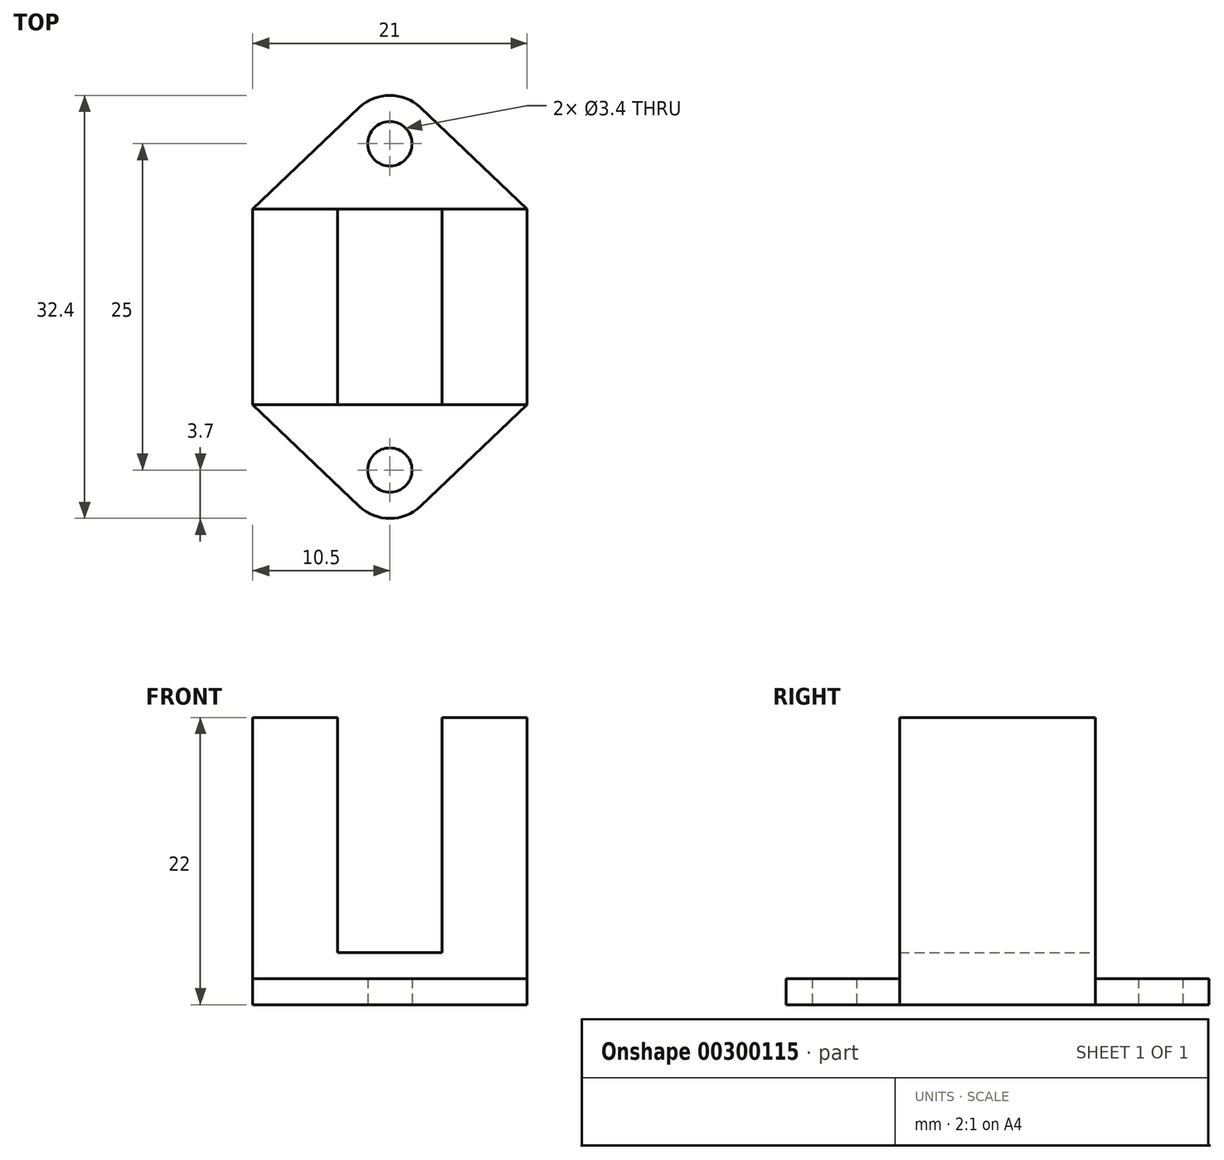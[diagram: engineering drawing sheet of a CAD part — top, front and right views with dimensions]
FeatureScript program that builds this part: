
annotation { "Feature Type Name" : "Feature", "Feature Type Description" : "" }
export const myFeature = defineFeature(function(context is Context, id is Id, definition is map)
    precondition{}
    {
        {
            var Q0;
            Q0=qCreatedBy(makeId("Top.planeOp"),FACE);
            var sketch = newSketch(context, id + "F0", { "sketchPlane" : qUnion([Q0])});
            skLineSegment(sketch, "E0.bottom", {"start": v(-9.75, 6.37) * mm, "end": v(9.75, 6.38) * mm});
            skLineSegment(sketch, "E0.top", {"start": v(-9.75, -6.38) * mm, "end": v(9.75, -6.38) * mm});
            skLineSegment(sketch, "E0.left", {"start": v(-9.75, 6.38) * mm, "end": v(-9.75, -6.38) * mm});
            skLineSegment(sketch, "E0.right", {"start": v(9.75, 6.38) * mm, "end": v(9.75, -6.38) * mm});
            skLineSegment(sketch, "E1.bottom", {"start": v(-10.5, 7.5) * mm, "end": v(10.5, 7.5) * mm});
            skLineSegment(sketch, "E1.top", {"start": v(-10.5, -7.5) * mm, "end": v(10.5, -7.5) * mm});
            skLineSegment(sketch, "E1.left", {"start": v(-10.5, 7.5) * mm, "end": v(-10.5, -7.5) * mm});
            skLineSegment(sketch, "E1.right", {"start": v(10.5, 7.5) * mm, "end": v(10.5, -7.5) * mm});
            skLineSegment(sketch, "E2", {"start": v(10.5, 0) * mm, "end": v(-10.5, 0) * mm, "construction": true});
            skLineSegment(sketch, "E3", {"start": v(0, 7.5) * mm, "end": v(0, -7.5) * mm, "construction": true});
            skLineSegment(sketch, "E4", {"start": v(9.75, 0) * mm, "end": v(-9.75, 0) * mm, "construction": true});
            skLineSegment(sketch, "E5", {"start": v(0, 6.38) * mm, "end": v(0, -6.38) * mm, "construction": true});
            skLineSegment(sketch, "E6", {"start": v(0, 7.5) * mm, "end": v(0, 17.5) * mm, "construction": true});
            skLineSegment(sketch, "E7", {"start": v(0, -7.5) * mm, "end": v(0, -17.5) * mm, "construction": true});
            skLineSegment(sketch, "E8", {"start": v(0, -17.5) * mm, "end": v(10.5, -7.5) * mm});
            skLineSegment(sketch, "E9", {"start": v(0, -17.5) * mm, "end": v(-10.5, -7.5) * mm});
            skLineSegment(sketch, "E10", {"start": v(-10.5, 7.5) * mm, "end": v(0, 17.5) * mm});
            skLineSegment(sketch, "E11", {"start": v(0, 17.5) * mm, "end": v(10.5, 7.5) * mm});
            skCircle(sketch, "E12", {"center": v(0, 12.5) * mm, "radius": 1.7 * mm});
            skCircle(sketch, "E13", {"center": v(0, -12.5) * mm, "radius": 1.7 * mm});
            skSolve(sketch);
        }
        {
            var Q0;
            Q0=makeQuery(id+"F0.imprint","IMPRINT",FACE,{"disambiguationData":[TD([[makeQuery(id+"F0.imprint","IMPRINT",EDGE,{"derivedFrom":sQuery(id+"F0.wireOp",EDGE,"E0.bottom")}),-1.0]])]});
            var Q1;
            Q1=makeQuery(id+"F0.imprint","IMPRINT",FACE,{"disambiguationData":[TD([[makeQuery(id+"F0.imprint","IMPRINT",EDGE,{"derivedFrom":sQuery(id+"F0.wireOp",EDGE,"E0.bottom")}),1.0]])]});
            extrude(context, id + "F1", {"entities" : qUnion([Q0, Q1]), "depth" : 22 * mm});
        }
        {
            var Q0;
            Q0=makeQuery(id+"F0.imprint","IMPRINT",FACE,{"disambiguationData":[TD([[makeQuery(id+"F0.imprint","IMPRINT",EDGE,{"derivedFrom":sQuery(id+"F0.wireOp",EDGE,"E1.top")}),-1.0]])]});
            var Q1;
            Q1=makeQuery(id+"F0.imprint","IMPRINT",FACE,{"disambiguationData":[TD([[makeQuery(id+"F0.imprint","IMPRINT",EDGE,{"derivedFrom":sQuery(id+"F0.wireOp",EDGE,"E1.bottom")}),1.0]])]});
            extrude(context, id + "F2", {"entities" : qUnion([Q0, Q1]), "operationType" : NewBodyOperationType.ADD, "depth" : 2 * mm});
        }
        {
            var Q0;
            Q0=makeQuery(id+"F2.opExtrude","SWEPT_EDGE",EDGE,{"disambiguationData":[OSD([sQuery(id+"F0.wireOp",EDGE,"E8"),sQuery(id+"F0.wireOp",EDGE,"E9")])]});
            var Q1;
            Q1=makeQuery(id+"F2.opExtrude","SWEPT_EDGE",EDGE,{"disambiguationData":[OSD([sQuery(id+"F0.wireOp",EDGE,"E10"),sQuery(id+"F0.wireOp",EDGE,"E11")])]});
            fillet(context, id + "F3", {"entities" : qUnion([Q0, Q1]), "radius" : 3.4 * mm, "tangentPropagation" : true, "allowEdgeOverflow" : false});
        }
        {
            var Q0;
            Q0=makeQuery(id+"F1.opExtrude","CAP_FACE",FACE,{"disambiguationData":[OSD([sQuery(id+"F0.wireOp",EDGE,"E1.bottom"),sQuery(id+"F0.wireOp",EDGE,"E1.top"),sQuery(id+"F0.wireOp",EDGE,"E1.left"),sQuery(id+"F0.wireOp",EDGE,"E1.right")])],"isStart":false});
            var sketch = newSketch(context, id + "F4", { "sketchPlane" : qUnion([Q0])});
            skLineSegment(sketch, "E14", {"start": v(0, -7.5) * mm, "end": v(0, 7.5) * mm, "construction": true});
            skLineSegment(sketch, "E15", {"start": v(0, -7.5) * mm, "end": v(-4, -7.5) * mm});
            skLineSegment(sketch, "E16", {"start": v(-4, -7.5) * mm, "end": v(-4, 7.5) * mm});
            skLineSegment(sketch, "E17", {"start": v(-4, 7.5) * mm, "end": v(4, 7.5) * mm});
            skLineSegment(sketch, "E18", {"start": v(4, 7.5) * mm, "end": v(4, -7.5) * mm});
            skLineSegment(sketch, "E19", {"start": v(4, -7.5) * mm, "end": v(0, -7.5) * mm});
            skSolve(sketch);
        }
        {
            var Q0;
            Q0=makeQuery(id+"F4.imprint","IMPRINT",FACE,{"disambiguationData":[TD([[makeQuery(id+"F4.imprint","IMPRINT",EDGE,{"derivedFrom":sQuery(id+"F4.wireOp",EDGE,"E15")}),1.0]])]});
            extrude(context, id + "F5", {"entities" : qUnion([Q0]), "operationType" : NewBodyOperationType.REMOVE, "oppositeDirection" : true, "depth" : 18 * mm});
        }
    });
